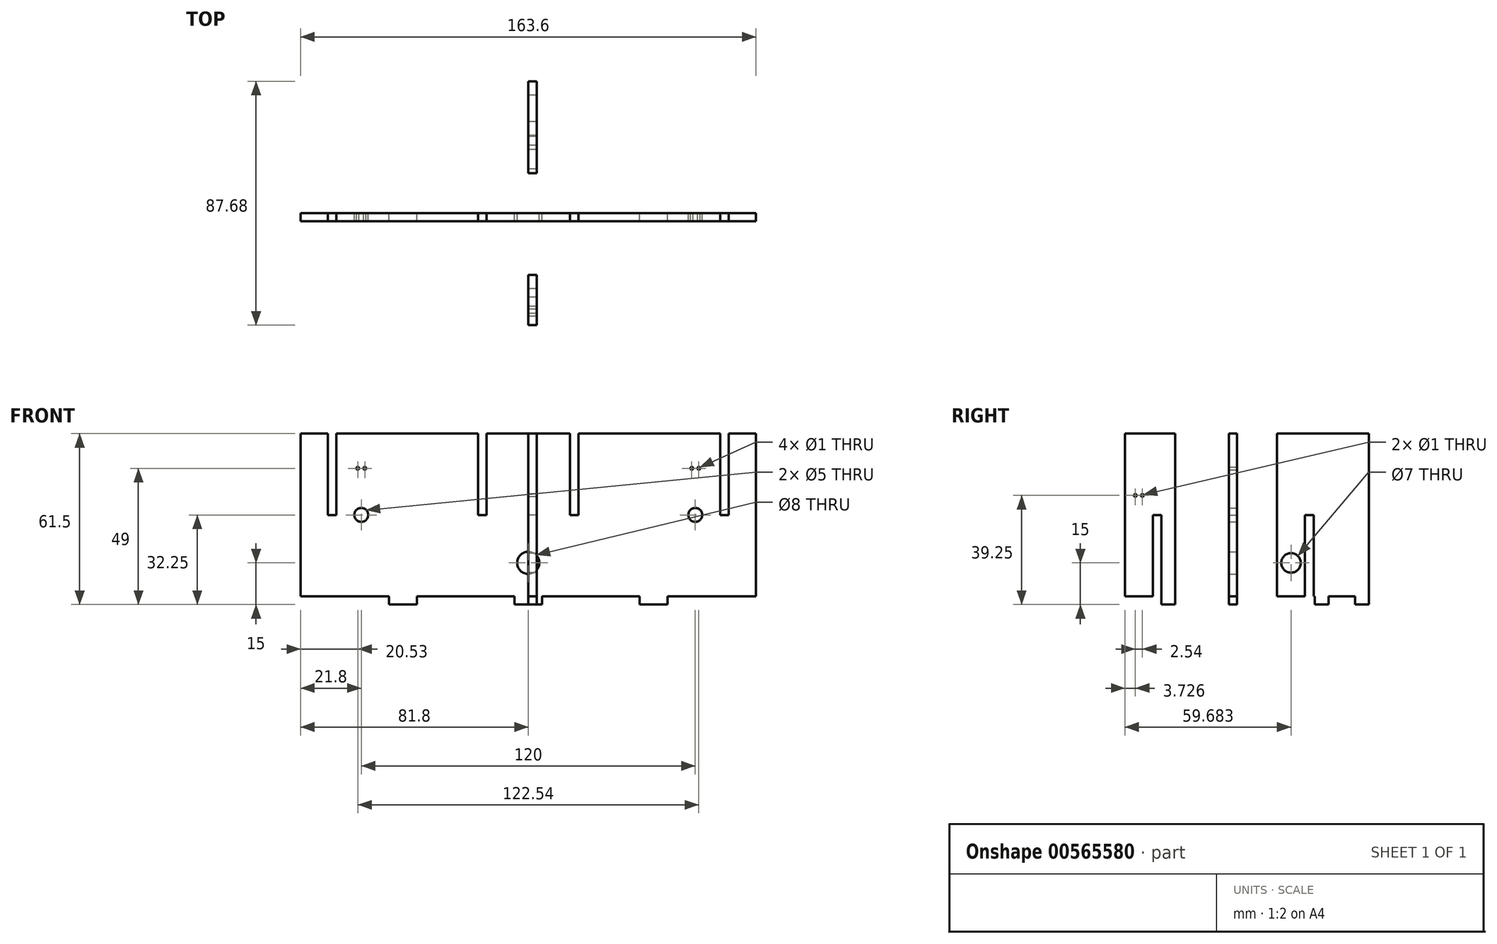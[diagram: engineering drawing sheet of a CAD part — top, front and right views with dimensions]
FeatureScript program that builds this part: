
annotation { "Feature Type Name" : "Feature", "Feature Type Description" : "" }
export const myFeature = defineFeature(function(context is Context, id is Id, definition is map)
    precondition{}
    {
        {
            var Q0;
            Q0=qCreatedBy(makeId("Front.planeOp"),FACE);
            var sketch = newSketch(context, id + "F0", { "sketchPlane" : qUnion([Q0])});
            skLineSegment(sketch, "E0.bottom", {"start": v(81.8, -29.25) * mm, "end": v(50, -29.25) * mm});
            skLineSegment(sketch, "E0.top", {"start": v(81.8, 29.25) * mm, "end": v(72.05, 29.25) * mm});
            skLineSegment(sketch, "E0.left", {"start": v(81.8, -29.25) * mm, "end": v(81.8, 29.25) * mm});
            skLineSegment(sketch, "E0.right", {"start": v(-81.8, -29.25) * mm, "end": v(-81.8, 29.25) * mm});
            skPoint(sketch, "E0.middle", {"position": v(0, 0) * mm});
            skLineSegment(sketch, "E1.top", {"start": v(72.05, 0) * mm, "end": v(68.95, 0) * mm});
            skLineSegment(sketch, "E1.left", {"start": v(72.05, 29.25) * mm, "end": v(72.05, 0) * mm});
            skLineSegment(sketch, "E1.right", {"start": v(68.95, 29.25) * mm, "end": v(68.95, 0) * mm});
            skLineSegment(sketch, "E2.top", {"start": v(-72.05, 0) * mm, "end": v(-68.95, 0) * mm});
            skLineSegment(sketch, "E2.left", {"start": v(-72.05, 29.25) * mm, "end": v(-72.05, 0) * mm});
            skLineSegment(sketch, "E2.right", {"start": v(-68.95, 29.25) * mm, "end": v(-68.95, 0) * mm});
            skLineSegment(sketch, "E3.top", {"start": v(18.05, 0) * mm, "end": v(14.95, 0) * mm});
            skLineSegment(sketch, "E3.left", {"start": v(18.05, 29.25) * mm, "end": v(18.05, 0) * mm});
            skLineSegment(sketch, "E3.right", {"start": v(14.95, 29.25) * mm, "end": v(14.95, 0) * mm});
            skLineSegment(sketch, "E4.top", {"start": v(-14.95, 0) * mm, "end": v(-18.05, 0) * mm});
            skLineSegment(sketch, "E4.left", {"start": v(-14.95, 29.25) * mm, "end": v(-14.95, 0) * mm});
            skLineSegment(sketch, "E4.right", {"start": v(-18.05, 29.25) * mm, "end": v(-18.05, 0) * mm});
            skLineSegment(sketch, "E5.trimOffspring", {"start": v(68.95, 29.25) * mm, "end": v(18.05, 29.25) * mm});
            skLineSegment(sketch, "E6.trimOffspring", {"start": v(14.95, 29.25) * mm, "end": v(-14.95, 29.25) * mm});
            skLineSegment(sketch, "E7.trimOffspring", {"start": v(-18.05, 29.25) * mm, "end": v(-68.95, 29.25) * mm});
            skLineSegment(sketch, "E8.trimOffspring", {"start": v(-72.05, 29.25) * mm, "end": v(-81.8, 29.25) * mm});
            skCircle(sketch, "E9", {"center": v(61.27, 16.75) * mm, "radius": 0.5 * mm});
            skCircle(sketch, "E10", {"center": v(58.73, 16.75) * mm, "radius": 0.5 * mm});
            skPoint(sketch, "E11", {"position": v(60, 16.75) * mm});
            skCircle(sketch, "E12", {"center": v(-61.27, 16.75) * mm, "radius": 0.5 * mm});
            skCircle(sketch, "E13", {"center": v(-58.73, 16.75) * mm, "radius": 0.5 * mm});
            skPoint(sketch, "E14", {"position": v(-60, 16.75) * mm});
            skCircle(sketch, "E15", {"center": v(0, -17.25) * mm, "radius": 4 * mm});
            skLineSegment(sketch, "E16.top", {"start": v(5, -32.25) * mm, "end": v(-5, -32.25) * mm});
            skLineSegment(sketch, "E16.left", {"start": v(5, -29.25) * mm, "end": v(5, -32.25) * mm});
            skLineSegment(sketch, "E16.right", {"start": v(-5, -29.25) * mm, "end": v(-5, -32.25) * mm});
            skLineSegment(sketch, "E17.top", {"start": v(-40, -32.25) * mm, "end": v(-50, -32.25) * mm});
            skLineSegment(sketch, "E17.left", {"start": v(-40, -29.25) * mm, "end": v(-40, -32.25) * mm});
            skLineSegment(sketch, "E17.right", {"start": v(-50, -29.25) * mm, "end": v(-50, -32.25) * mm});
            skLineSegment(sketch, "E18.top", {"start": v(40, -32.25) * mm, "end": v(50, -32.25) * mm});
            skLineSegment(sketch, "E18.left", {"start": v(40, -29.25) * mm, "end": v(40, -32.25) * mm});
            skLineSegment(sketch, "E18.right", {"start": v(50, -29.25) * mm, "end": v(50, -32.25) * mm});
            skLineSegment(sketch, "E19.trimOffspring", {"start": v(40, -29.25) * mm, "end": v(5, -29.25) * mm});
            skLineSegment(sketch, "E20.trimOffspring", {"start": v(-5, -29.25) * mm, "end": v(-40, -29.25) * mm});
            skLineSegment(sketch, "E21.trimOffspring", {"start": v(-50, -29.25) * mm, "end": v(-81.8, -29.25) * mm});
            skCircle(sketch, "E22", {"center": v(60, 0) * mm, "radius": 2.5 * mm});
            skCircle(sketch, "E23", {"center": v(-60, 0) * mm, "radius": 2.5 * mm});
            skSolve(sketch);
        }
        {
            var Q0;
            Q0 = qSketchRegion(id + "F0", true);
            extrude(context, id + "F1", {"entities" : qUnion([Q0]), "depth" : 3 * mm, "offsetDistance" : 25 * mm});
        }
        {
            var Q0;
            Q0=qCreatedBy(makeId("Right.planeOp"),FACE);
            var sketch = newSketch(context, id + "F2", { "sketchPlane" : qUnion([Q0])});
            skLineSegment(sketch, "E24.bottom", {"start": v(-22.33, 29.25) * mm, "end": v(-40.33, 29.25) * mm});
            skLineSegment(sketch, "E24.top", {"start": v(-30.33, -29.25) * mm, "end": v(-40.33, -29.25) * mm});
            skLineSegment(sketch, "E24.left", {"start": v(-22.33, 29.25) * mm, "end": v(-22.33, -29.25) * mm});
            skLineSegment(sketch, "E24.right", {"start": v(-40.33, 29.25) * mm, "end": v(-40.33, -29.25) * mm});
            skLineSegment(sketch, "E25.top", {"start": v(-22.33, -32.25) * mm, "end": v(-27.23, -32.25) * mm});
            skLineSegment(sketch, "E25.left", {"start": v(-22.33, -29.25) * mm, "end": v(-22.33, -32.25) * mm});
            skLineSegment(sketch, "E25.right", {"start": v(-27.23, -29.25) * mm, "end": v(-27.23, -32.25) * mm});
            skLineSegment(sketch, "E26.top", {"start": v(-27.23, 0) * mm, "end": v(-30.33, 0) * mm});
            skLineSegment(sketch, "E26.left", {"start": v(-27.23, -29.25) * mm, "end": v(-27.23, 0) * mm});
            skLineSegment(sketch, "E26.right", {"start": v(-30.33, -29.25) * mm, "end": v(-30.33, 0) * mm});
            skCircle(sketch, "E27", {"center": v(-36.6, 7) * mm, "radius": 0.5 * mm});
            skCircle(sketch, "E28", {"center": v(-34.06, 7) * mm, "radius": 0.5 * mm});
            skPoint(sketch, "E29", {"position": v(-35.33, 7) * mm});
            skSolve(sketch);
        }
        {
            var Q0;
            Q0=qCreatedBy(makeId("Right.planeOp"),FACE);
            var sketch = newSketch(context, id + "F3", { "sketchPlane" : qUnion([Q0])});
            skLineSegment(sketch, "E30.bottom", {"start": v(14.35, 29.25) * mm, "end": v(47.35, 29.25) * mm});
            skLineSegment(sketch, "E30.top", {"start": v(14.35, -29.25) * mm, "end": v(24.35, -29.25) * mm});
            skLineSegment(sketch, "E30.left", {"start": v(14.35, 29.25) * mm, "end": v(14.35, -29.25) * mm});
            skLineSegment(sketch, "E30.right", {"start": v(47.35, 29.25) * mm, "end": v(47.35, -29.25) * mm});
            skLineSegment(sketch, "E31.top", {"start": v(27.85, -32.25) * mm, "end": v(32.85, -32.25) * mm});
            skLineSegment(sketch, "E31.left", {"start": v(27.85, -29.25) * mm, "end": v(27.85, -32.25) * mm});
            skLineSegment(sketch, "E31.right", {"start": v(32.85, -29.25) * mm, "end": v(32.85, -32.25) * mm});
            skLineSegment(sketch, "E32.top", {"start": v(47.35, -32.25) * mm, "end": v(42.35, -32.25) * mm});
            skLineSegment(sketch, "E32.left", {"start": v(47.35, -29.25) * mm, "end": v(47.35, -32.25) * mm});
            skLineSegment(sketch, "E32.right", {"start": v(42.35, -29.25) * mm, "end": v(42.35, -32.25) * mm});
            skLineSegment(sketch, "E33.top", {"start": v(24.35, 0) * mm, "end": v(27.45, 0) * mm});
            skLineSegment(sketch, "E33.left", {"start": v(24.35, -29.25) * mm, "end": v(24.35, 0) * mm});
            skLineSegment(sketch, "E33.right", {"start": v(27.45, -29.25) * mm, "end": v(27.45, 0) * mm});
            skLineSegment(sketch, "E34.trimOffspring", {"start": v(27.45, -29.25) * mm, "end": v(27.85, -29.25) * mm});
            skLineSegment(sketch, "E35.trimOffspring", {"start": v(32.85, -29.25) * mm, "end": v(42.35, -29.25) * mm});
            skCircle(sketch, "E36", {"center": v(19.35, -17.25) * mm, "radius": 3.5 * mm});
            skPoint(sketch, "E36.centerSnap0", {"position": v(19.35, -29.25) * mm});
            skPoint(sketch, "E37.centerSnap0", {"position": v(37.6, -29.25) * mm});
            skSolve(sketch);
        }
        {
            var Q0;
            Q0=makeQuery(id+"F2.imprint","IMPRINT",FACE,{"disambiguationData":[TD([[makeQuery(id+"F2.imprint","IMPRINT",EDGE,{"derivedFrom":sQuery(id+"F2.wireOp",EDGE,"E24.bottom")}),1.0]])]});
            extrude(context, id + "F4", {"entities" : qUnion([Q0]), "depth" : 3 * mm, "offsetDistance" : 25 * mm});
        }
        {
            var Q0;
            Q0=makeQuery(id+"F3.imprint","IMPRINT",FACE,{"disambiguationData":[TD([[makeQuery(id+"F3.imprint","IMPRINT",EDGE,{"derivedFrom":sQuery(id+"F3.wireOp",EDGE,"E30.bottom")}),-1.0]])]});
            var Q1;
            Q1=makeQuery(id+"F3.imprint","IMPRINT",FACE,{"disambiguationData":[TD([[makeQuery(id+"F3.imprint","IMPRINT",EDGE,{"derivedFrom":sQuery(id+"F3.wireOp",EDGE,"E32.top")}),-1.0]])]});
            var Q2;
            Q2=makeQuery(id+"F3.imprint","IMPRINT",FACE,{"disambiguationData":[TD([[makeQuery(id+"F3.imprint","IMPRINT",EDGE,{"derivedFrom":sQuery(id+"F3.wireOp",EDGE,"E31.top")}),1.0]])]});
            extrude(context, id + "F5", {"entities" : qUnion([Q0, Q1, Q2]), "depth" : 3 * mm, "offsetDistance" : 25 * mm});
        }
    });
